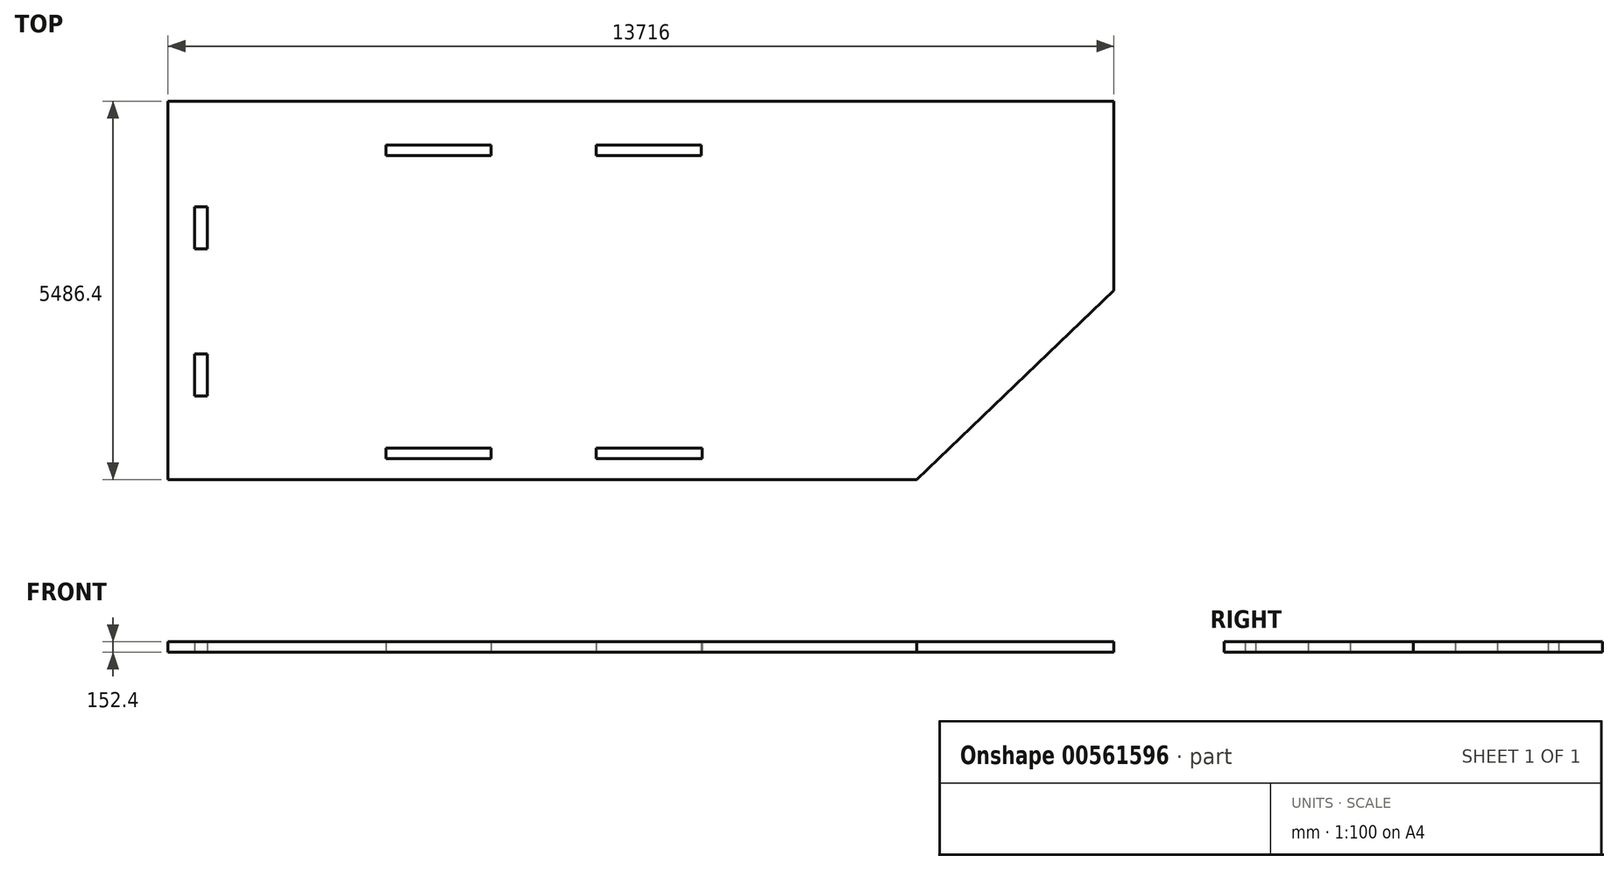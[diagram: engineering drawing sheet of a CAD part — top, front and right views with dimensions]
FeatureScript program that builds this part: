
annotation { "Feature Type Name" : "Feature", "Feature Type Description" : "" }
export const myFeature = defineFeature(function(context is Context, id is Id, definition is map)
    precondition{}
    {
        {
            var Q0;
            Q0=qCreatedBy(makeId("Top.planeOp"),FACE);
            var sketch = newSketch(context, id + "F0", { "sketchPlane" : qUnion([Q0])});
            skLineSegment(sketch, "E0.bottom", {"start": v(-385.65, 5334) * mm, "end": v(13330.35, 5334) * mm});
            skLineSegment(sketch, "E0.top", {"start": v(-385.65, -152.4) * mm, "end": v(13330.35, -152.4) * mm});
            skLineSegment(sketch, "E0.left", {"start": v(-385.65, 5334) * mm, "end": v(-385.65, -152.4) * mm});
            skLineSegment(sketch, "E0.right", {"start": v(13330.35, 5334) * mm, "end": v(13330.35, -152.4) * mm});
            skLineSegment(sketch, "E1.bottom", {"start": v(0, 3805.33) * mm, "end": v(182.88, 3805.33) * mm});
            skLineSegment(sketch, "E1.top", {"start": v(0, 3195.73) * mm, "end": v(182.88, 3195.73) * mm});
            skLineSegment(sketch, "E1.left", {"start": v(0, 3805.33) * mm, "end": v(0, 3195.73) * mm});
            skLineSegment(sketch, "E1.right", {"start": v(182.88, 3805.33) * mm, "end": v(182.88, 3195.73) * mm});
            skLineSegment(sketch, "E2.bottom", {"start": v(0, 1062.13) * mm, "end": v(182.88, 1062.13) * mm});
            skLineSegment(sketch, "E2.top", {"start": v(0, 1671.73) * mm, "end": v(182.88, 1671.73) * mm});
            skLineSegment(sketch, "E2.left", {"start": v(0, 1062.13) * mm, "end": v(0, 1671.73) * mm});
            skLineSegment(sketch, "E2.right", {"start": v(182.88, 1062.13) * mm, "end": v(182.88, 1671.73) * mm});
            skPoint(sketch, "E3.start.orphan", {"position": v(0, 5334) * mm});
            skLineSegment(sketch, "E4", {"start": v(182.88, 3805.33) * mm, "end": v(182.88, 5334) * mm, "construction": true});
            skLineSegment(sketch, "E5", {"start": v(182.88, 1062.13) * mm, "end": v(182.88, -152.4) * mm, "construction": true});
            skLineSegment(sketch, "E6.bottom", {"start": v(2773.68, 4695.07) * mm, "end": v(4297.68, 4695.07) * mm});
            skLineSegment(sketch, "E6.top", {"start": v(2773.68, 4542.67) * mm, "end": v(4297.68, 4542.67) * mm});
            skLineSegment(sketch, "E6.left", {"start": v(2773.68, 4695.07) * mm, "end": v(2773.68, 4542.67) * mm});
            skLineSegment(sketch, "E6.right", {"start": v(4297.68, 4695.07) * mm, "end": v(4297.68, 4542.67) * mm});
            skPoint(sketch, "E7.end.orphan", {"position": v(3378.21, 5181.6) * mm});
            skPoint(sketch, "E8.start.orphan", {"position": v(182.88, 5181.6) * mm});
            skPoint(sketch, "E9.end.orphan", {"position": v(2773.68, 148.95) * mm});
            skPoint(sketch, "E9.start.orphan", {"position": v(182.88, 0) * mm});
            skPoint(sketch, "E10.end.orphan", {"position": v(3378.21, 0) * mm});
            skPoint(sketch, "E10.start.orphan", {"position": v(3378.21, -152.4) * mm});
            skLineSegment(sketch, "E11", {"start": v(2773.68, 148.95) * mm, "end": v(4297.68, 148.95) * mm});
            skLineSegment(sketch, "E12", {"start": v(4297.68, 148.95) * mm, "end": v(4297.68, 301.35) * mm});
            skLineSegment(sketch, "E13", {"start": v(4297.68, 301.35) * mm, "end": v(2773.68, 301.35) * mm});
            skLineSegment(sketch, "E14", {"start": v(2773.68, 301.35) * mm, "end": v(2773.68, 148.95) * mm});
            skLineSegment(sketch, "E15.bottom", {"start": v(5821.68, 4542.67) * mm, "end": v(7345.68, 4542.67) * mm});
            skLineSegment(sketch, "E15.top", {"start": v(5821.68, 4695.07) * mm, "end": v(7345.68, 4695.07) * mm});
            skLineSegment(sketch, "E15.left", {"start": v(5821.68, 4542.67) * mm, "end": v(5821.68, 4695.07) * mm});
            skLineSegment(sketch, "E15.right", {"start": v(7345.68, 4542.67) * mm, "end": v(7345.68, 4695.07) * mm});
            skPoint(sketch, "E16.left.start.orphan", {"position": v(5821.68, 152.4) * mm});
            skPoint(sketch, "E17.end.orphan", {"position": v(7345.68, 0) * mm});
            skLineSegment(sketch, "E18.bottom", {"start": v(5821.68, 301.35) * mm, "end": v(7360.02, 301.35) * mm});
            skLineSegment(sketch, "E18.top", {"start": v(5821.68, 148.95) * mm, "end": v(7360.02, 148.95) * mm});
            skLineSegment(sketch, "E18.left", {"start": v(5821.68, 301.35) * mm, "end": v(5821.68, 148.95) * mm});
            skLineSegment(sketch, "E18.right", {"start": v(7360.02, 301.35) * mm, "end": v(7360.02, 148.95) * mm});
            skSolve(sketch);
        }
        {
            var Q0;
            Q0=qSketchRegion(id+"F0",true);
            extrude(context, id + "F1", {"entities" : qUnion([Q0]), "depth" : 152.4 * mm, "offsetDistance" : 30.48 * mm});
        }
        {
            var Q0;
            Q0=makeQuery(id+"F1.opExtrude","CAP_FACE",FACE,{"disambiguationData":[OSD([sQuery(id+"F0.wireOp",EDGE,"E0.bottom"),sQuery(id+"F0.wireOp",EDGE,"E0.top"),sQuery(id+"F0.wireOp",EDGE,"E0.left"),sQuery(id+"F0.wireOp",EDGE,"E0.right")])],"isStart":false});
            var sketch = newSketch(context, id + "F2", { "sketchPlane" : qUnion([Q0])});
            skLineSegment(sketch, "E19", {"start": v(13330.35, 2590.8) * mm, "end": v(10471.07, 5334) * mm});
            skLineSegment(sketch, "E20", {"start": v(10471.07, 5334) * mm, "end": v(13330.35, 2590.8) * mm});
            skLineSegment(sketch, "E21", {"start": v(13330.35, 2590.8) * mm, "end": v(10471.07, -152.4) * mm});
            skLineSegment(sketch, "E22", {"start": v(10471.07, 5334) * mm, "end": v(13330.35, 5334) * mm});
            skLineSegment(sketch, "E23", {"start": v(13330.35, 5334) * mm, "end": v(13330.35, 2590.8) * mm});
            skLineSegment(sketch, "E24", {"start": v(10471.07, -152.4) * mm, "end": v(13330.35, -152.4) * mm});
            skLineSegment(sketch, "E25", {"start": v(13330.35, -152.4) * mm, "end": v(13330.35, 2590.8) * mm});
            skSolve(sketch);
        }
        {
            var Q0;
            Q0=makeQuery(id+"F2.imprint","IMPRINT",FACE,{"disambiguationData":[TD([[makeQuery(id+"F2.imprint","IMPRINT",EDGE,{"derivedFrom":sQuery(id+"F2.wireOp",EDGE,"E21")}),1.0]])]});
            var Q1;
            Q1=makeQuery(id+"F2.imprint","IMPRINT",FACE,{"disambiguationData":[TD([[makeQuery(id+"F2.imprint","IMPRINT",EDGE,{"derivedFrom":sQuery(id+"F2.wireOp",EDGE,"E20")}),1.0]])]});
            extrude(context, id + "F3", {"entities" : qUnion([Q0, Q1]), "operationType" : NewBodyOperationType.REMOVE, "endBound" : BoundingType.THROUGH_ALL, "oppositeDirection" : true, "depth" : 152.4 * mm, "offsetDistance" : 30.48 * mm});
        }
    });
